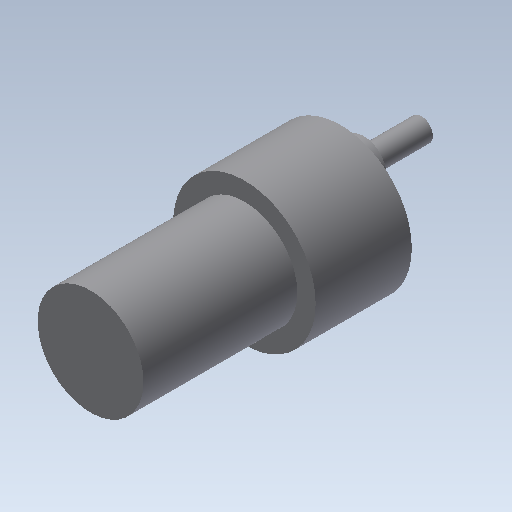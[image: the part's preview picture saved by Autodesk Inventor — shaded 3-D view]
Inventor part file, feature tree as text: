
AUTODESK INVENTOR PART (.ipt)
format: ipt  version: 2020.3 (Build 243373000, 373)  size: 140,288 bytes
history: native  units: mm
features: other x6, sketch x6, extrude x5, hole x1
ambient origin geometry x8: Origin, YZ Plane, XZ Plane, XY Plane, X Axis, Y Axis, Z Axis, Center Point
bodies: Body1 (feature_tree)
feature tree (18):
  other  "ソリッド1"
  extrude  "押し出し1"  Depth=37.0mm
  extrude  "押し出し2"  Depth=25.0mm TaperAngle=0.0deg
  extrude  "押し出し3"  Depth=27.5mm
  extrude  "押し出し4"  Depth=40.0mm TaperAngle=0.0deg
  hole  "Hole1"  [1 undecoded]
  other  "作業点1"
  other  "作業点2"
  other  "作業平面1"
  extrude  "押し出し5"  Depth=7.0mm
  sketch  "スケッチ1"
  sketch  "スケッチ2"
  sketch  "スケッチ3"
  sketch  "スケッチ4"
  sketch  "スケッチ5"
  other  "作業点3"
  other  "作業点4"
  sketch  "スケッチ6"
note: 1 required parameter value undecoded (feature->parameter linkage not recoverable at this tier; creation-order binding heuristic only, values carry confidence <= 0.55)
